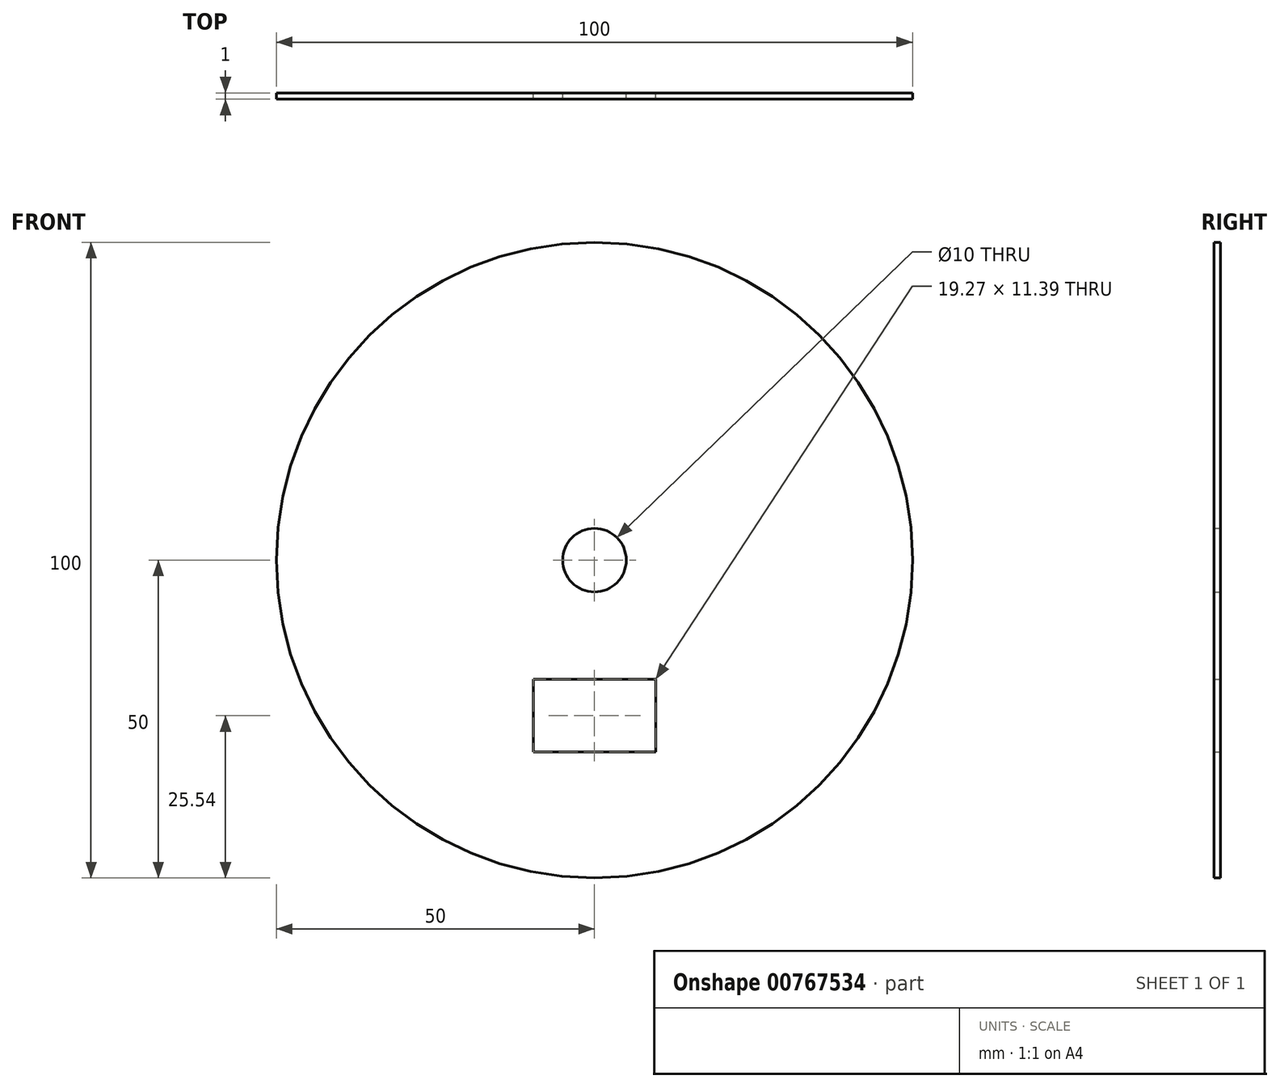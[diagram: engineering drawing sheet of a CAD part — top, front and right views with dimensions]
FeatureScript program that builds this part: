
annotation { "Feature Type Name" : "Feature", "Feature Type Description" : "" }
export const myFeature = defineFeature(function(context is Context, id is Id, definition is map)
    precondition{}
    {
        {
            var Q0;
            Q0=qCreatedBy(makeId("Front.planeOp"),FACE);
            var sketch = newSketch(context, id + "F0", { "sketchPlane" : qUnion([Q0])});
            skCircle(sketch, "E0", {"center": v(0, 0) * mm, "radius": 50 * mm});
            skCircle(sketch, "E1", {"center": v(0, 0) * mm, "radius": 5 * mm});
            skLineSegment(sketch, "E2.bottom", {"start": v(-9.63, -18.76) * mm, "end": v(9.63, -18.76) * mm});
            skLineSegment(sketch, "E2.top", {"start": v(-9.63, -30.15) * mm, "end": v(9.63, -30.15) * mm});
            skLineSegment(sketch, "E2.left", {"start": v(-9.63, -18.76) * mm, "end": v(-9.63, -30.15) * mm});
            skLineSegment(sketch, "E2.right", {"start": v(9.63, -18.76) * mm, "end": v(9.63, -30.15) * mm});
            skPoint(sketch, "E2.middle", {"position": v(0, -24.46) * mm});
            skSolve(sketch);
        }
        {
            var Q0;
            Q0=makeQuery(id+"F0.imprint","IMPRINT",FACE,{"disambiguationData":[TD([[makeQuery(id+"F0.imprint","IMPRINT",EDGE,{"derivedFrom":sQuery(id+"F0.wireOp",EDGE,"E0")}),1.0]])]});
            extrude(context, id + "F1", {"entities" : qUnion([Q0]), "endBound" : BoundingType.SYMMETRIC, "depth" : 1 * mm, "offsetDistance" : 25 * mm});
        }
    });
